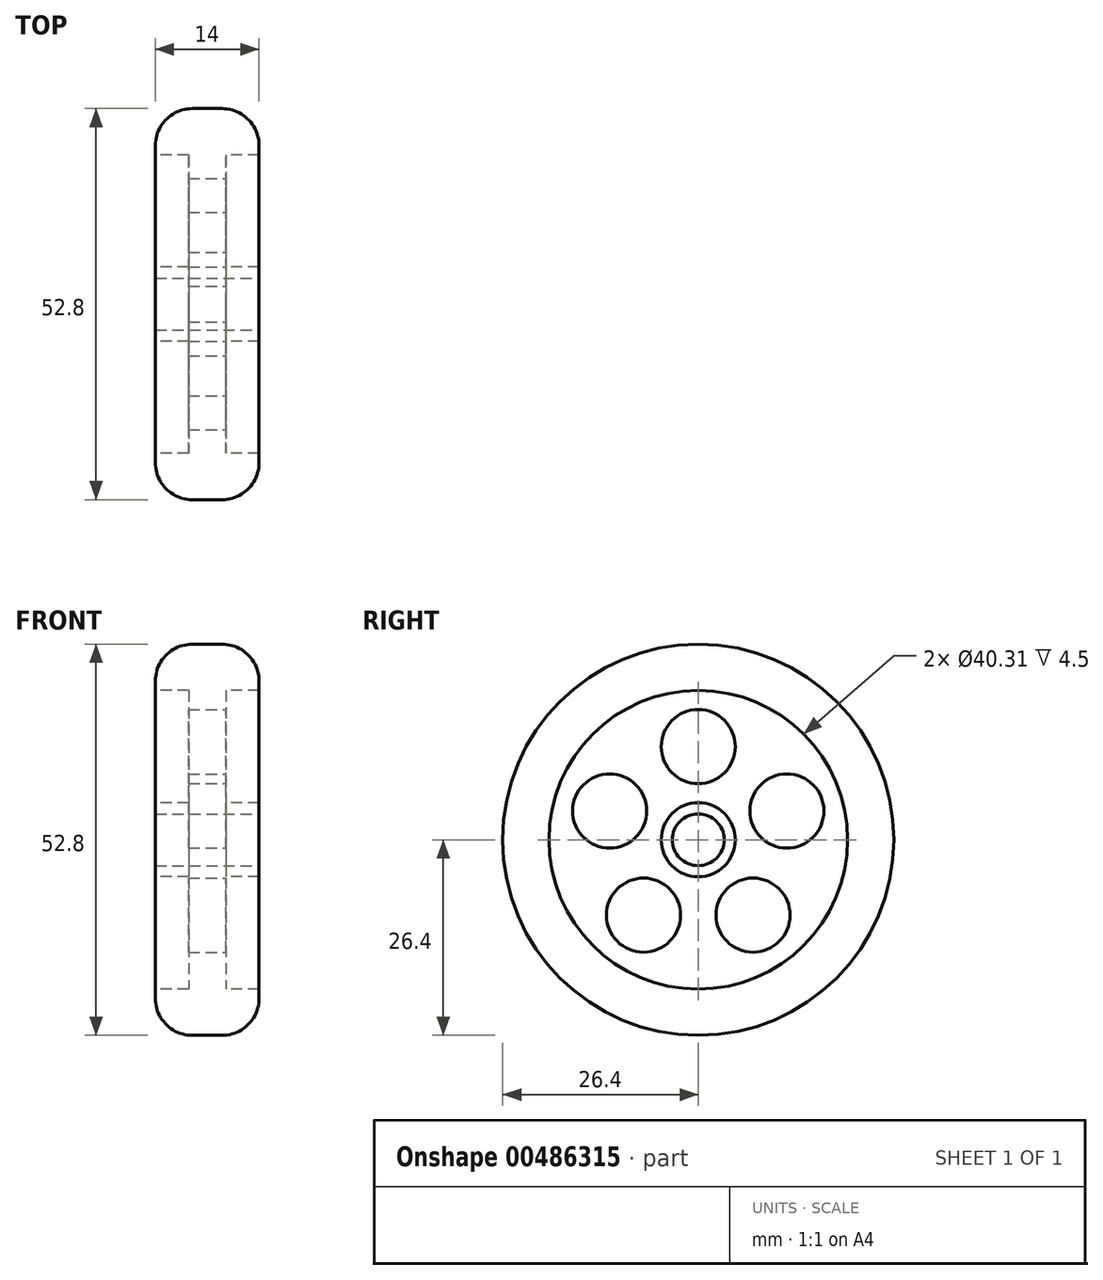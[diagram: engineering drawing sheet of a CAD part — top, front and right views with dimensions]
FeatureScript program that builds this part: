
annotation { "Feature Type Name" : "Feature", "Feature Type Description" : "" }
export const myFeature = defineFeature(function(context is Context, id is Id, definition is map)
    precondition{}
    {
        {
            var Q0;
            Q0=qCreatedBy(makeId("Front.planeOp"),FACE);
            var sketch = newSketch(context, id + "F0", { "sketchPlane" : qUnion([Q0])});
            skLineSegment(sketch, "E0", {"start": v(0, 0) * mm, "end": v(14, 0) * mm});
            skLineSegment(sketch, "E1", {"start": v(14, 0) * mm, "end": v(14, 5) * mm});
            skLineSegment(sketch, "E2", {"start": v(14, 5) * mm, "end": v(9.5, 5) * mm});
            skLineSegment(sketch, "E3", {"start": v(9.5, 5) * mm, "end": v(9.5, 20.15) * mm});
            skLineSegment(sketch, "E4", {"start": v(9.5, 20.15) * mm, "end": v(14, 20.15) * mm});
            skLineSegment(sketch, "E5", {"start": v(14, 20.15) * mm, "end": v(14, 26.4) * mm});
            skLineSegment(sketch, "E6", {"start": v(14, 26.4) * mm, "end": v(0, 26.4) * mm});
            skLineSegment(sketch, "E7", {"start": v(0, 26.4) * mm, "end": v(0, 20.15) * mm});
            skLineSegment(sketch, "E8", {"start": v(0, 20.15) * mm, "end": v(4.5, 20.15) * mm});
            skLineSegment(sketch, "E9", {"start": v(4.5, 20.15) * mm, "end": v(4.5, 5) * mm});
            skLineSegment(sketch, "E10", {"start": v(4.5, 5) * mm, "end": v(0, 5) * mm});
            skLineSegment(sketch, "E11", {"start": v(0, 5) * mm, "end": v(0, 0) * mm});
            skSolve(sketch);
        }
        {
            var Q0;
            Q0 = qSketchRegion(id + "F0", true);
            var Q1;
            Q1=sQuery(id+"F0.wireOp",EDGE,"E0");
            revolve(context, id + "F1", {"entities" : qUnion([Q0]), "axis" : qUnion([Q1]), "revolveType" : RevolveType.FULL});
        }
        {
            var Q0;
            Q0=makeQuery(id+"F1.opRevolve","SWEPT_FACE",FACE,{"disambiguationData":[OSD([sQuery(id+"F0.wireOp",EDGE,"E3")])]});
            var sketch = newSketch(context, id + "F2", { "sketchPlane" : qUnion([Q0])});
            skCircle(sketch, "E12", {"center": v(0, 12.57) * mm, "radius": 5 * mm});
            skCircle(sketch, "E13.1.0", {"center": v(-11.96, 3.89) * mm, "radius": 5 * mm});
            skCircle(sketch, "E13.2.0", {"center": v(-7.4, -10.17) * mm, "radius": 5 * mm});
            skCircle(sketch, "E13.3.0", {"center": v(7.4, -10.17) * mm, "radius": 5 * mm});
            skCircle(sketch, "E13.4.0", {"center": v(11.96, 3.89) * mm, "radius": 5 * mm});
            skPoint(sketch, "E13.center", {"position": v(0, 0) * mm});
            skSolve(sketch);
        }
        {
            var Q0;
            Q0=sQuery(id+"F2.wireOp",VERTEX,"E12.center");
            var Q1;
            Q1=sQuery(id+"F2.wireOp",VERTEX,"E13.1.0.center");
            var Q2;
            Q2=sQuery(id+"F2.wireOp",VERTEX,"E13.2.0.center");
            var Q3;
            Q3=sQuery(id+"F2.wireOp",VERTEX,"E13.3.0.center");
            var Q4;
            Q4=sQuery(id+"F2.wireOp",VERTEX,"E13.4.0.center");
            var Q5;
            Q5=makeQuery(id+"F1.opRevolve","SWEPT_BODY",BODY,{"disambiguationData":[OSD([sQuery(id+"F0.wireOp",EDGE,"E0"),sQuery(id+"F0.wireOp",EDGE,"E1"),sQuery(id+"F0.wireOp",EDGE,"E2"),sQuery(id+"F0.wireOp",EDGE,"E3"),sQuery(id+"F0.wireOp",EDGE,"E4"),sQuery(id+"F0.wireOp",EDGE,"E5"),sQuery(id+"F0.wireOp",EDGE,"E6"),sQuery(id+"F0.wireOp",EDGE,"E7"),sQuery(id+"F0.wireOp",EDGE,"E8"),sQuery(id+"F0.wireOp",EDGE,"E9"),sQuery(id+"F0.wireOp",EDGE,"E10"),sQuery(id+"F0.wireOp",EDGE,"E11")])]});
            hole(context, id + "F3", {"style" : HoleStyle.SIMPLE, "endStyle" : HoleEndStyle.THROUGH, "holeDiameter" : 10 * mm, "isTappedThrough" : true, "tappedDepth" : 12 * mm, "tapClearance" : 3, "locations" : qUnion([Q0, Q1, Q2, Q3, Q4]), "scope" : qUnion([Q5])});
        }
        {
            var Q0;
            Q0=makeQuery(id+"F1.opRevolve","SWEPT_EDGE",EDGE,{"disambiguationData":[OSD([sQuery(id+"F0.wireOp",EDGE,"E5"),sQuery(id+"F0.wireOp",EDGE,"E6")])]});
            var Q1;
            Q1=makeQuery(id+"F1.opRevolve","SWEPT_EDGE",EDGE,{"disambiguationData":[OSD([sQuery(id+"F0.wireOp",EDGE,"E6"),sQuery(id+"F0.wireOp",EDGE,"E7")])]});
            fillet(context, id + "F4", {"entities" : qUnion([Q0, Q1]), "radius" : 5 * mm, "tangentPropagation" : true, "allowEdgeOverflow" : false});
        }
        {
            var Q0;
            Q0=makeQuery(id+"F1.opRevolve","SWEPT_FACE",FACE,{"disambiguationData":[OSD([sQuery(id+"F0.wireOp",EDGE,"E1")])]});
            var sketch = newSketch(context, id + "F5", { "sketchPlane" : qUnion([Q0])});
            skCircle(sketch, "E14", {"center": v(0, 0) * mm, "radius": 3.5 * mm});
            skSolve(sketch);
        }
        {
            var Q0;
            Q0=sQuery(id+"F5.wireOp",VERTEX,"E14.center");
            var Q1;
            Q1=makeQuery(id+"F1.opRevolve","SWEPT_BODY",BODY,{"disambiguationData":[OSD([sQuery(id+"F0.wireOp",EDGE,"E0"),sQuery(id+"F0.wireOp",EDGE,"E1"),sQuery(id+"F0.wireOp",EDGE,"E2"),sQuery(id+"F0.wireOp",EDGE,"E3"),sQuery(id+"F0.wireOp",EDGE,"E4"),sQuery(id+"F0.wireOp",EDGE,"E5"),sQuery(id+"F0.wireOp",EDGE,"E6"),sQuery(id+"F0.wireOp",EDGE,"E7"),sQuery(id+"F0.wireOp",EDGE,"E8"),sQuery(id+"F0.wireOp",EDGE,"E9"),sQuery(id+"F0.wireOp",EDGE,"E10"),sQuery(id+"F0.wireOp",EDGE,"E11")])]});
            hole(context, id + "F6", {"style" : HoleStyle.SIMPLE, "endStyle" : HoleEndStyle.THROUGH, "holeDiameter" : 7 * mm, "isTappedThrough" : true, "tappedDepth" : 12 * mm, "tapClearance" : 3, "locations" : qUnion([Q0]), "scope" : qUnion([Q1])});
        }
    });
